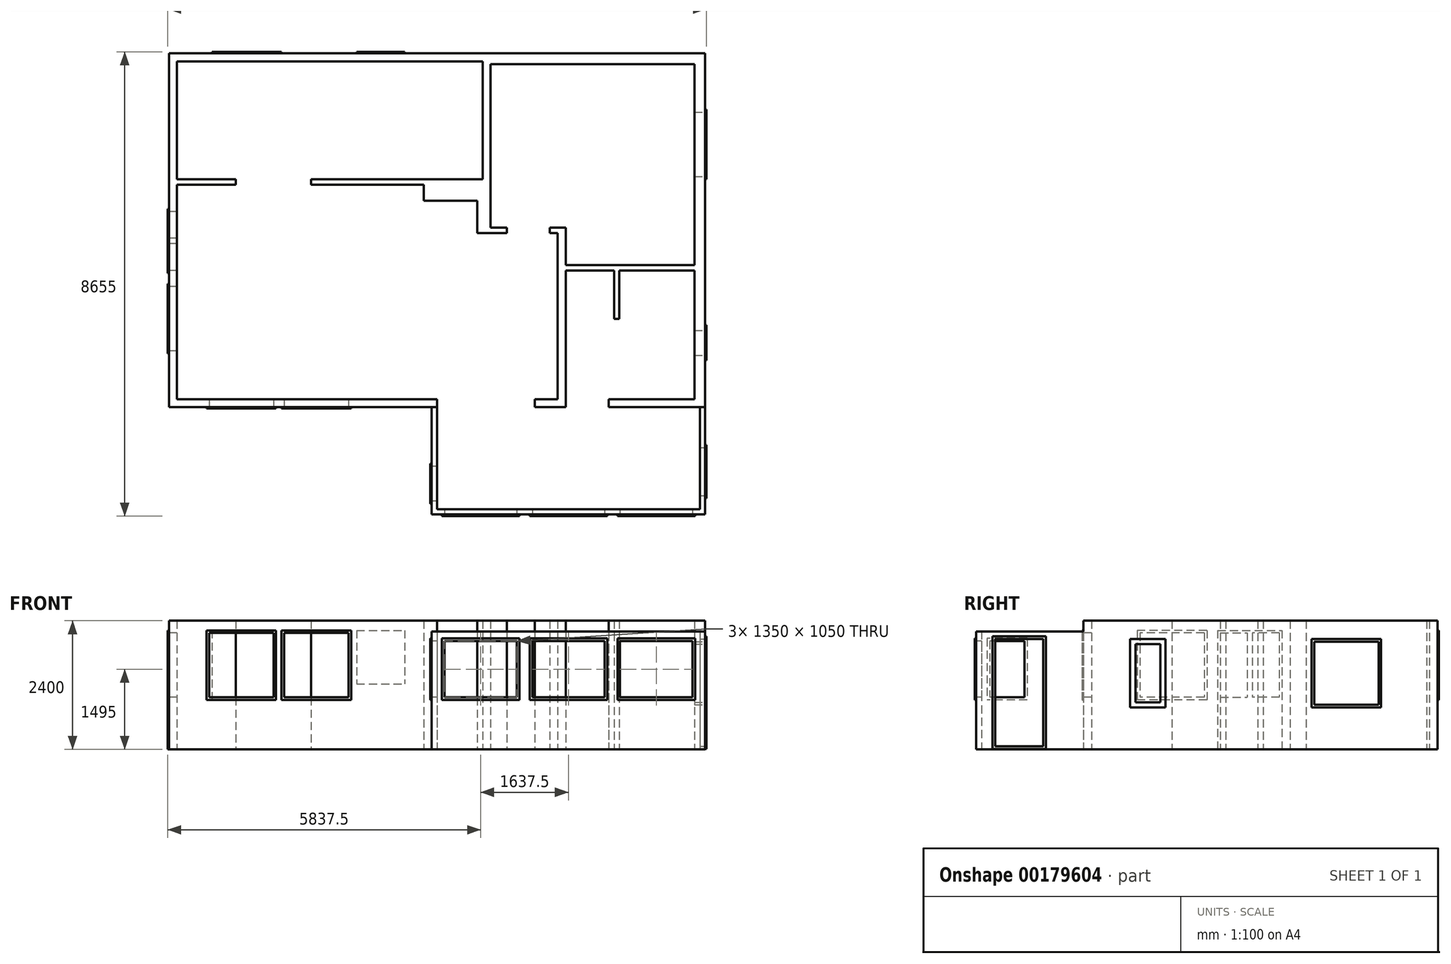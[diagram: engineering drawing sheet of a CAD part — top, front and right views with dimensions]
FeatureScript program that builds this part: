
annotation { "Feature Type Name" : "Feature", "Feature Type Description" : "" }
export const myFeature = defineFeature(function(context is Context, id is Id, definition is map)
    precondition{}
    {
        {
            var Q0;
            Q0=qCreatedBy(makeId("Top.planeOp"),FACE);
            var sketch = newSketch(context, id + "F0", { "sketchPlane" : qUnion([Q0])});
            skLineSegment(sketch, "E0", {"start": v(0, 0) * mm, "end": v(0, 6600) * mm});
            skLineSegment(sketch, "E1", {"start": v(0, 6600) * mm, "end": v(10000, 6600) * mm});
            skLineSegment(sketch, "E2", {"start": v(10000, 6600) * mm, "end": v(10000, 0) * mm});
            skLineSegment(sketch, "E3", {"start": v(10000, 0) * mm, "end": v(8200, 0) * mm});
            skLineSegment(sketch, "E4", {"start": v(8200, 0) * mm, "end": v(8200, 150) * mm});
            skLineSegment(sketch, "E5", {"start": v(8200, 150) * mm, "end": v(9800, 150) * mm});
            skLineSegment(sketch, "E6", {"start": v(9800, 150) * mm, "end": v(9800, 2550) * mm});
            skLineSegment(sketch, "E7", {"start": v(9800, 2550) * mm, "end": v(8400, 2550) * mm});
            skLineSegment(sketch, "E8", {"start": v(8400, 2550) * mm, "end": v(8400, 1650) * mm});
            skLineSegment(sketch, "E9", {"start": v(8400, 1650) * mm, "end": v(8300, 1650) * mm});
            skLineSegment(sketch, "E10", {"start": v(8300, 1650) * mm, "end": v(8300, 2550) * mm});
            skLineSegment(sketch, "E11", {"start": v(8300, 2550) * mm, "end": v(7400, 2550) * mm});
            skLineSegment(sketch, "E12", {"start": v(6820, 150) * mm, "end": v(7250, 150) * mm});
            skLineSegment(sketch, "E13", {"start": v(7250, 150) * mm, "end": v(7250, 3250) * mm});
            skLineSegment(sketch, "E14", {"start": v(7250, 3250) * mm, "end": v(7100, 3250) * mm});
            skLineSegment(sketch, "E15", {"start": v(7100, 3250) * mm, "end": v(7100, 3350) * mm});
            skLineSegment(sketch, "E16", {"start": v(7100, 3350) * mm, "end": v(7400, 3350) * mm});
            skLineSegment(sketch, "E17", {"start": v(7400, 3350) * mm, "end": v(7400, 2650) * mm});
            skLineSegment(sketch, "E18", {"start": v(7400, 2650) * mm, "end": v(9800, 2650) * mm});
            skLineSegment(sketch, "E19", {"start": v(9800, 2650) * mm, "end": v(9800, 6400) * mm});
            skLineSegment(sketch, "E20", {"start": v(6000, 3350) * mm, "end": v(6300, 3350) * mm});
            skLineSegment(sketch, "E21", {"start": v(6300, 3350) * mm, "end": v(6300, 3250) * mm});
            skLineSegment(sketch, "E22", {"start": v(6300, 3250) * mm, "end": v(5750, 3250) * mm});
            skLineSegment(sketch, "E23", {"start": v(5750, 3250) * mm, "end": v(5750, 3850) * mm});
            skLineSegment(sketch, "E24", {"start": v(4750, 3850) * mm, "end": v(4750, 4150) * mm});
            skLineSegment(sketch, "E25", {"start": v(2650, 4250) * mm, "end": v(5850, 4250) * mm});
            skLineSegment(sketch, "E26", {"start": v(5850, 4250) * mm, "end": v(5850, 6450) * mm});
            skLineSegment(sketch, "E27", {"start": v(5850, 6450) * mm, "end": v(150, 6450) * mm});
            skLineSegment(sketch, "E28", {"start": v(150, 6450) * mm, "end": v(150, 4250) * mm});
            skLineSegment(sketch, "E29", {"start": v(150, 4250) * mm, "end": v(1250, 4250) * mm});
            skLineSegment(sketch, "E30", {"start": v(1250, 4250) * mm, "end": v(1250, 4150) * mm});
            skLineSegment(sketch, "E31", {"start": v(1250, 4150) * mm, "end": v(150, 4150) * mm});
            skLineSegment(sketch, "E32", {"start": v(150, 4150) * mm, "end": v(150, 150) * mm});
            skLineSegment(sketch, "E33", {"start": v(150, 150) * mm, "end": v(5000, 150) * mm});
            skLineSegment(sketch, "E34", {"start": v(5000, 150) * mm, "end": v(5000, 0) * mm});
            skLineSegment(sketch, "E35", {"start": v(5000, 0) * mm, "end": v(0, 0) * mm});
            skLineSegment(sketch, "E36", {"start": v(4750, 3850) * mm, "end": v(5750, 3850) * mm});
            skLineSegment(sketch, "E37", {"start": v(6000, 6400) * mm, "end": v(9800, 6400) * mm});
            skLineSegment(sketch, "E38", {"start": v(6000, 6400) * mm, "end": v(6000, 3350) * mm});
            skLineSegment(sketch, "E39", {"start": v(7400, 0) * mm, "end": v(7400, 2550) * mm});
            skLineSegment(sketch, "E40", {"start": v(6820, 150) * mm, "end": v(6820, 0) * mm});
            skLineSegment(sketch, "E41", {"start": v(6820, 0) * mm, "end": v(7400, 0) * mm});
            skLineSegment(sketch, "E42", {"start": v(2650, 4150) * mm, "end": v(4750, 4150) * mm});
            skLineSegment(sketch, "E43", {"start": v(2650, 4250) * mm, "end": v(2650, 4150) * mm});
            skSolve(sketch);
        }
        {
            var Q0;
            Q0 = qSketchRegion(id + "F0", true);
            extrude(context, id + "F1", {"entities" : qUnion([Q0]), "depth" : 2400 * mm});
        }
        {
            var Q0;
            Q0=qCreatedBy(makeId("Top.planeOp"),FACE);
            var sketch = newSketch(context, id + "F2", { "sketchPlane" : qUnion([Q0])});
            skLineSegment(sketch, "E44", {"start": v(10000, 0) * mm, "end": v(10000, -2000) * mm});
            skLineSegment(sketch, "E45", {"start": v(10000, -2000) * mm, "end": v(4900, -2000) * mm});
            skLineSegment(sketch, "E46", {"start": v(4900, -2000) * mm, "end": v(4900, 0) * mm});
            skLineSegment(sketch, "E47", {"start": v(4900, 0) * mm, "end": v(5000, 0) * mm});
            skLineSegment(sketch, "E48", {"start": v(5000, 0) * mm, "end": v(5000, -1900) * mm});
            skLineSegment(sketch, "E49", {"start": v(5000, -1900) * mm, "end": v(9900, -1900) * mm});
            skLineSegment(sketch, "E50", {"start": v(9900, -1900) * mm, "end": v(9900, 0) * mm});
            skLineSegment(sketch, "E51", {"start": v(9900, 0) * mm, "end": v(10000, 0) * mm});
            skSolve(sketch);
        }
        {
            var Q0;
            Q0 = qSketchRegion(id + "F2", true);
            extrude(context, id + "F3", {"entities" : qUnion([Q0]), "operationType" : NewBodyOperationType.ADD, "depth" : 2200 * mm});
        }
        {
            var Q0;
            Q0=makeQuery(id+"F3.opExtrude","SWEPT_FACE",FACE,{"disambiguationData":[OSD([sQuery(id+"F2.wireOp",EDGE,"E45")])]});
            var sketch = newSketch(context, id + "F4", { "sketchPlane" : qUnion([Q0])});
            skLineSegment(sketch, "E52.bottom", {"start": v(6725, 2070) * mm, "end": v(8175, 2070) * mm});
            skLineSegment(sketch, "E52.top", {"start": v(6725, 920) * mm, "end": v(8175, 920) * mm});
            skLineSegment(sketch, "E52.left", {"start": v(6725, 2070) * mm, "end": v(6725, 920) * mm});
            skLineSegment(sketch, "E52.right", {"start": v(8175, 2070) * mm, "end": v(8175, 920) * mm});
            skPoint(sketch, "E53.endSnap0", {"position": v(7450, 2200) * mm});
            skLineSegment(sketch, "E54.bottom", {"start": v(6537.5, 2070) * mm, "end": v(5087.5, 2070) * mm});
            skLineSegment(sketch, "E54.top", {"start": v(6537.5, 920) * mm, "end": v(5087.5, 920) * mm});
            skLineSegment(sketch, "E54.left", {"start": v(6537.5, 2070) * mm, "end": v(6537.5, 920) * mm});
            skLineSegment(sketch, "E54.right", {"start": v(5087.5, 2070) * mm, "end": v(5087.5, 920) * mm});
            skLineSegment(sketch, "E55.bottom", {"start": v(8362.5, 2070) * mm, "end": v(9812.5, 2070) * mm});
            skLineSegment(sketch, "E55.top", {"start": v(8362.5, 920) * mm, "end": v(9812.5, 920) * mm});
            skLineSegment(sketch, "E55.left", {"start": v(8362.5, 2070) * mm, "end": v(8362.5, 920) * mm});
            skLineSegment(sketch, "E55.right", {"start": v(9812.5, 2070) * mm, "end": v(9812.5, 920) * mm});
            skSolve(sketch);
        }
        {
            var Q0;
            Q0=makeQuery(id+"F4.imprint","IMPRINT",FACE,{"disambiguationData":[TD([[makeQuery(id+"F4.imprint","IMPRINT",EDGE,{"derivedFrom":sQuery(id+"F4.wireOp",EDGE,"E54.bottom")}),1.0]])]});
            var Q1;
            Q1=makeQuery(id+"F4.imprint","IMPRINT",FACE,{"disambiguationData":[TD([[makeQuery(id+"F4.imprint","IMPRINT",EDGE,{"derivedFrom":sQuery(id+"F4.wireOp",EDGE,"E52.bottom")}),-1.0]])]});
            var Q2;
            Q2=makeQuery(id+"F4.imprint","IMPRINT",FACE,{"disambiguationData":[TD([[makeQuery(id+"F4.imprint","IMPRINT",EDGE,{"derivedFrom":sQuery(id+"F4.wireOp",EDGE,"E55.bottom")}),-1.0]])]});
            extrude(context, id + "F5", {"entities" : qUnion([Q0, Q1, Q2]), "operationType" : NewBodyOperationType.ADD, "depth" : 30 * mm});
        }
        {
            var Q0;
            Q0=makeQuery(id+"F5.opExtrude","CAP_FACE",FACE,{"disambiguationData":[OSD([sQuery(id+"F4.wireOp",EDGE,"E54.bottom"),sQuery(id+"F4.wireOp",EDGE,"E54.top"),sQuery(id+"F4.wireOp",EDGE,"E54.left"),sQuery(id+"F4.wireOp",EDGE,"E54.right")])],"isStart":false});
            var sketch = newSketch(context, id + "F6", { "sketchPlane" : qUnion([Q0])});
            skLineSegment(sketch, "E56.bottom", {"start": v(5137.5, 2020) * mm, "end": v(6487.5, 2020) * mm});
            skLineSegment(sketch, "E56.top", {"start": v(5137.5, 970) * mm, "end": v(6487.5, 970) * mm});
            skLineSegment(sketch, "E56.left", {"start": v(5137.5, 2020) * mm, "end": v(5137.5, 970) * mm});
            skLineSegment(sketch, "E56.right", {"start": v(6487.5, 2020) * mm, "end": v(6487.5, 970) * mm});
            skLineSegment(sketch, "E57.bottom", {"start": v(6775, 2020) * mm, "end": v(8125, 2020) * mm});
            skLineSegment(sketch, "E57.top", {"start": v(6775, 970) * mm, "end": v(8125, 970) * mm});
            skLineSegment(sketch, "E57.left", {"start": v(6775, 2020) * mm, "end": v(6775, 970) * mm});
            skLineSegment(sketch, "E57.right", {"start": v(8125, 2020) * mm, "end": v(8125, 970) * mm});
            skLineSegment(sketch, "E58.bottom", {"start": v(8412.5, 2020) * mm, "end": v(9762.5, 2020) * mm});
            skLineSegment(sketch, "E58.top", {"start": v(8412.5, 970) * mm, "end": v(9762.5, 970) * mm});
            skLineSegment(sketch, "E58.left", {"start": v(8412.5, 2020) * mm, "end": v(8412.5, 970) * mm});
            skLineSegment(sketch, "E58.right", {"start": v(9762.5, 2020) * mm, "end": v(9762.5, 970) * mm});
            skSolve(sketch);
        }
        {
            var Q0;
            Q0 = qSketchRegion(id + "F6", true);
            extrude(context, id + "F7", {"entities" : qUnion([Q0]), "operationType" : NewBodyOperationType.REMOVE, "endBound" : BoundingType.UP_TO_NEXT, "oppositeDirection" : true, "depth" : 25 * mm});
        }
        {
            var Q0;
            Q0=makeQuery(id+"F3.boolean.opBoolean","MERGE",FACE,{"derivedFrom":[makeQuery(id+"F1.opExtrude","SWEPT_FACE",FACE,{"disambiguationData":[OSD([sQuery(id+"F0.wireOp",EDGE,"E2")])]}),makeQuery(id+"F3.opExtrude","SWEPT_FACE",FACE,{"disambiguationData":[OSD([sQuery(id+"F2.wireOp",EDGE,"E44")])]})]});
            var sketch = newSketch(context, id + "F8", { "sketchPlane" : qUnion([Q0])});
            skLineSegment(sketch, "E59.bottom", {"start": v(-1700, 2110) * mm, "end": v(-700, 2110) * mm});
            skLineSegment(sketch, "E59.top", {"start": v(-1700, 10) * mm, "end": v(-700, 10) * mm});
            skLineSegment(sketch, "E59.left", {"start": v(-1700, 2110) * mm, "end": v(-1700, 10) * mm});
            skLineSegment(sketch, "E59.right", {"start": v(-700, 2110) * mm, "end": v(-700, 10) * mm});
            skSolve(sketch);
        }
        {
            var Q0;
            Q0 = qSketchRegion(id + "F8", true);
            extrude(context, id + "F9", {"entities" : qUnion([Q0]), "operationType" : NewBodyOperationType.ADD, "depth" : 25 * mm});
        }
        {
            var Q0;
            Q0=makeQuery(id+"F9.opExtrude","CAP_FACE",FACE,{"disambiguationData":[OSD([sQuery(id+"F8.wireOp",EDGE,"E59.bottom"),sQuery(id+"F8.wireOp",EDGE,"E59.top"),sQuery(id+"F8.wireOp",EDGE,"E59.left"),sQuery(id+"F8.wireOp",EDGE,"E59.right")])],"isStart":false});
            var sketch = newSketch(context, id + "F10", { "sketchPlane" : qUnion([Q0])});
            skLineSegment(sketch, "E60.bottom", {"start": v(-1650, 2060) * mm, "end": v(-750, 2060) * mm});
            skLineSegment(sketch, "E60.top", {"start": v(-1650, 60) * mm, "end": v(-750, 60) * mm});
            skLineSegment(sketch, "E60.left", {"start": v(-1650, 2060) * mm, "end": v(-1650, 60) * mm});
            skLineSegment(sketch, "E60.right", {"start": v(-750, 2060) * mm, "end": v(-750, 60) * mm});
            skSolve(sketch);
        }
        {
            var Q0;
            Q0 = qSketchRegion(id + "F10", true);
            extrude(context, id + "F11", {"entities" : qUnion([Q0]), "operationType" : NewBodyOperationType.REMOVE, "oppositeDirection" : true, "depth" : 125 * mm});
        }
        {
            var Q0;
            Q0=makeQuery(id+"F3.opExtrude","SWEPT_FACE",FACE,{"disambiguationData":[OSD([sQuery(id+"F2.wireOp",EDGE,"E46")])]});
            var sketch = newSketch(context, id + "F12", { "sketchPlane" : qUnion([Q0])});
            skLineSegment(sketch, "E61.bottom", {"start": v(1050, 2070) * mm, "end": v(1800, 2070) * mm});
            skLineSegment(sketch, "E61.top", {"start": v(1050, 920) * mm, "end": v(1800, 920) * mm});
            skLineSegment(sketch, "E61.left", {"start": v(1050, 2070) * mm, "end": v(1050, 920) * mm});
            skLineSegment(sketch, "E61.right", {"start": v(1800, 2070) * mm, "end": v(1800, 920) * mm});
            skSolve(sketch);
        }
        {
            var Q0;
            Q0 = qSketchRegion(id + "F12", true);
            extrude(context, id + "F13", {"entities" : qUnion([Q0]), "operationType" : NewBodyOperationType.ADD, "depth" : 25 * mm});
        }
        {
            var Q0;
            Q0=makeQuery(id+"F13.opExtrude","CAP_FACE",FACE,{"disambiguationData":[OSD([sQuery(id+"F12.wireOp",EDGE,"E61.bottom"),sQuery(id+"F12.wireOp",EDGE,"E61.top"),sQuery(id+"F12.wireOp",EDGE,"E61.left"),sQuery(id+"F12.wireOp",EDGE,"E61.right")])],"isStart":false});
            var sketch = newSketch(context, id + "F14", { "sketchPlane" : qUnion([Q0])});
            skLineSegment(sketch, "E62.bottom", {"start": v(1100, 2020) * mm, "end": v(1750, 2020) * mm});
            skLineSegment(sketch, "E62.top", {"start": v(1100, 970) * mm, "end": v(1750, 970) * mm});
            skLineSegment(sketch, "E62.left", {"start": v(1100, 2020) * mm, "end": v(1100, 970) * mm});
            skLineSegment(sketch, "E62.right", {"start": v(1750, 2020) * mm, "end": v(1750, 970) * mm});
            skSolve(sketch);
        }
        {
            var Q0;
            Q0 = qSketchRegion(id + "F14", true);
            extrude(context, id + "F15", {"entities" : qUnion([Q0]), "operationType" : NewBodyOperationType.REMOVE, "endBound" : BoundingType.UP_TO_NEXT, "oppositeDirection" : true, "depth" : 25 * mm});
        }
        {
            var Q0;
            Q0=makeQuery(id+"F3.boolean.opBoolean","MERGE",FACE,{"derivedFrom":[makeQuery(id+"F1.opExtrude","SWEPT_FACE",FACE,{"disambiguationData":[OSD([sQuery(id+"F0.wireOp",EDGE,"E2")])]}),makeQuery(id+"F3.opExtrude","SWEPT_FACE",FACE,{"disambiguationData":[OSD([sQuery(id+"F2.wireOp",EDGE,"E44")])]})]});
            var sketch = newSketch(context, id + "F16", { "sketchPlane" : qUnion([Q0])});
            skLineSegment(sketch, "E63.bottom", {"start": v(870, 2060) * mm, "end": v(1530, 2060) * mm});
            skLineSegment(sketch, "E63.top", {"start": v(870, 780) * mm, "end": v(1530, 780) * mm});
            skLineSegment(sketch, "E63.left", {"start": v(870, 2060) * mm, "end": v(870, 780) * mm});
            skLineSegment(sketch, "E63.right", {"start": v(1530, 2060) * mm, "end": v(1530, 780) * mm});
            skSolve(sketch);
        }
        {
            var Q0;
            Q0 = qSketchRegion(id + "F16", true);
            extrude(context, id + "F17", {"entities" : qUnion([Q0]), "operationType" : NewBodyOperationType.ADD, "depth" : 25 * mm});
        }
        {
            var Q0;
            Q0=makeQuery(id+"F17.opExtrude","CAP_FACE",FACE,{"disambiguationData":[OSD([sQuery(id+"F16.wireOp",EDGE,"E63.bottom"),sQuery(id+"F16.wireOp",EDGE,"E63.top"),sQuery(id+"F16.wireOp",EDGE,"E63.left"),sQuery(id+"F16.wireOp",EDGE,"E63.right")])],"isStart":false});
            var sketch = newSketch(context, id + "F18", { "sketchPlane" : qUnion([Q0])});
            skLineSegment(sketch, "E64.bottom", {"start": v(970, 1960) * mm, "end": v(1430, 1960) * mm});
            skLineSegment(sketch, "E64.top", {"start": v(970, 880) * mm, "end": v(1430, 880) * mm});
            skLineSegment(sketch, "E64.left", {"start": v(970, 1960) * mm, "end": v(970, 880) * mm});
            skLineSegment(sketch, "E64.right", {"start": v(1430, 1960) * mm, "end": v(1430, 880) * mm});
            skSolve(sketch);
        }
        {
            var Q0;
            Q0 = qSketchRegion(id + "F18", true);
            extrude(context, id + "F19", {"entities" : qUnion([Q0]), "operationType" : NewBodyOperationType.REMOVE, "endBound" : BoundingType.UP_TO_NEXT, "oppositeDirection" : true, "depth" : 25 * mm});
        }
        {
            var Q0;
            Q0=makeQuery(id+"F3.boolean.opBoolean","MERGE",FACE,{"derivedFrom":[makeQuery(id+"F1.opExtrude","SWEPT_FACE",FACE,{"disambiguationData":[OSD([sQuery(id+"F0.wireOp",EDGE,"E2")])]}),makeQuery(id+"F3.opExtrude","SWEPT_FACE",FACE,{"disambiguationData":[OSD([sQuery(id+"F2.wireOp",EDGE,"E44")])]})]});
            var sketch = newSketch(context, id + "F20", { "sketchPlane" : qUnion([Q0])});
            skLineSegment(sketch, "E65.bottom", {"start": v(5550, 2060) * mm, "end": v(4250, 2060) * mm});
            skLineSegment(sketch, "E65.top", {"start": v(5550, 780) * mm, "end": v(4250, 780) * mm});
            skLineSegment(sketch, "E65.left", {"start": v(5550, 2060) * mm, "end": v(5550, 780) * mm});
            skLineSegment(sketch, "E65.right", {"start": v(4250, 2060) * mm, "end": v(4250, 780) * mm});
            skSolve(sketch);
        }
        {
            var Q0;
            Q0 = qSketchRegion(id + "F20", true);
            extrude(context, id + "F21", {"entities" : qUnion([Q0]), "operationType" : NewBodyOperationType.ADD, "depth" : 25 * mm});
        }
        {
            var Q0;
            Q0=makeQuery(id+"F21.opExtrude","CAP_FACE",FACE,{"disambiguationData":[OSD([sQuery(id+"F20.wireOp",EDGE,"E65.bottom"),sQuery(id+"F20.wireOp",EDGE,"E65.top"),sQuery(id+"F20.wireOp",EDGE,"E65.left"),sQuery(id+"F20.wireOp",EDGE,"E65.right")])],"isStart":false});
            var sketch = newSketch(context, id + "F22", { "sketchPlane" : qUnion([Q0])});
            skLineSegment(sketch, "E66.bottom", {"start": v(4300, 2010) * mm, "end": v(5500, 2010) * mm});
            skLineSegment(sketch, "E66.top", {"start": v(4300, 830) * mm, "end": v(5500, 830) * mm});
            skLineSegment(sketch, "E66.left", {"start": v(4300, 2010) * mm, "end": v(4300, 830) * mm});
            skLineSegment(sketch, "E66.right", {"start": v(5500, 2010) * mm, "end": v(5500, 830) * mm});
            skSolve(sketch);
        }
        {
            var Q0;
            Q0 = qSketchRegion(id + "F22", true);
            extrude(context, id + "F23", {"entities" : qUnion([Q0]), "operationType" : NewBodyOperationType.REMOVE, "endBound" : BoundingType.UP_TO_NEXT, "oppositeDirection" : true, "depth" : 25 * mm});
        }
        {
            var Q0;
            Q0=makeQuery(id+"F1.opExtrude","SWEPT_FACE",FACE,{"disambiguationData":[OSD([sQuery(id+"F0.wireOp",EDGE,"E35")])]});
            var sketch = newSketch(context, id + "F24", { "sketchPlane" : qUnion([Q0])});
            skLineSegment(sketch, "E67.bottom", {"start": v(2100, 2220) * mm, "end": v(3400, 2220) * mm});
            skLineSegment(sketch, "E67.top", {"start": v(2100, 920) * mm, "end": v(3400, 920) * mm});
            skLineSegment(sketch, "E67.left", {"start": v(2100, 2220) * mm, "end": v(2100, 920) * mm});
            skLineSegment(sketch, "E67.right", {"start": v(3400, 2220) * mm, "end": v(3400, 920) * mm});
            skLineSegment(sketch, "E68.bottom", {"start": v(2000, 2220) * mm, "end": v(700, 2220) * mm});
            skLineSegment(sketch, "E68.top", {"start": v(2000, 920) * mm, "end": v(700, 920) * mm});
            skLineSegment(sketch, "E68.left", {"start": v(2000, 2220) * mm, "end": v(2000, 920) * mm});
            skLineSegment(sketch, "E68.right", {"start": v(700, 2220) * mm, "end": v(700, 920) * mm});
            skSolve(sketch);
        }
        {
            var Q0;
            Q0 = qSketchRegion(id + "F24", true);
            extrude(context, id + "F25", {"entities" : qUnion([Q0]), "operationType" : NewBodyOperationType.ADD, "depth" : 25 * mm});
        }
        {
            var Q0;
            Q0=makeQuery(id+"F25.opExtrude","CAP_FACE",FACE,{"disambiguationData":[OSD([sQuery(id+"F24.wireOp",EDGE,"E67.bottom"),sQuery(id+"F24.wireOp",EDGE,"E67.top"),sQuery(id+"F24.wireOp",EDGE,"E67.left"),sQuery(id+"F24.wireOp",EDGE,"E67.right")])],"isStart":false});
            var sketch = newSketch(context, id + "F26", { "sketchPlane" : qUnion([Q0])});
            skLineSegment(sketch, "E69.bottom", {"start": v(2150, 2170) * mm, "end": v(3350, 2170) * mm});
            skLineSegment(sketch, "E69.top", {"start": v(2150, 970) * mm, "end": v(3350, 970) * mm});
            skLineSegment(sketch, "E69.left", {"start": v(2150, 2170) * mm, "end": v(2150, 970) * mm});
            skLineSegment(sketch, "E69.right", {"start": v(3350, 2170) * mm, "end": v(3350, 970) * mm});
            skLineSegment(sketch, "E70.bottom", {"start": v(750, 2170) * mm, "end": v(1950, 2170) * mm});
            skLineSegment(sketch, "E70.top", {"start": v(750, 970) * mm, "end": v(1950, 970) * mm});
            skLineSegment(sketch, "E70.left", {"start": v(750, 2170) * mm, "end": v(750, 970) * mm});
            skLineSegment(sketch, "E70.right", {"start": v(1950, 2170) * mm, "end": v(1950, 970) * mm});
            skSolve(sketch);
        }
        {
            var Q0;
            Q0 = qSketchRegion(id + "F26", true);
            extrude(context, id + "F27", {"entities" : qUnion([Q0]), "operationType" : NewBodyOperationType.REMOVE, "endBound" : BoundingType.UP_TO_NEXT, "oppositeDirection" : true, "depth" : 25 * mm});
        }
        {
            var Q0;
            Q0=makeQuery(id+"F1.opExtrude","SWEPT_FACE",FACE,{"disambiguationData":[OSD([sQuery(id+"F0.wireOp",EDGE,"E1")])]});
            var sketch = newSketch(context, id + "F28", { "sketchPlane" : qUnion([Q0])});
            skLineSegment(sketch, "E71.bottom", {"start": v(-2100, 2220) * mm, "end": v(-800, 2220) * mm});
            skLineSegment(sketch, "E71.top", {"start": v(-2100, 920) * mm, "end": v(-800, 920) * mm});
            skLineSegment(sketch, "E71.left", {"start": v(-2100, 2220) * mm, "end": v(-2100, 920) * mm});
            skLineSegment(sketch, "E71.right", {"start": v(-800, 2220) * mm, "end": v(-800, 920) * mm});
            skLineSegment(sketch, "E72.bottom", {"start": v(-3500, 2220) * mm, "end": v(-4400, 2220) * mm});
            skLineSegment(sketch, "E72.top", {"start": v(-3500, 1220) * mm, "end": v(-4400, 1220) * mm});
            skLineSegment(sketch, "E72.left", {"start": v(-3500, 2220) * mm, "end": v(-3500, 1220) * mm});
            skLineSegment(sketch, "E72.right", {"start": v(-4400, 2220) * mm, "end": v(-4400, 1220) * mm});
            skSolve(sketch);
        }
        {
            var Q0;
            Q0 = qSketchRegion(id + "F28", true);
            var Q1;
            Q1=makeQuery(id+"F28.imprint","IMPRINT",FACE,{"disambiguationData":[TD([[makeQuery(id+"F28.imprint","IMPRINT",EDGE,{"derivedFrom":sQuery(id+"F28.wireOp",EDGE,"E72.bottom")}),1.0]])]});
            extrude(context, id + "F29", {"entities" : qUnion([Q0, Q1]), "operationType" : NewBodyOperationType.ADD, "depth" : 25 * mm});
        }
        {
            var Q0;
            Q0=makeQuery(id+"F1.opExtrude","SWEPT_FACE",FACE,{"disambiguationData":[OSD([sQuery(id+"F0.wireOp",EDGE,"E0")])]});
            var sketch = newSketch(context, id + "F30", { "sketchPlane" : qUnion([Q0])});
            skLineSegment(sketch, "E73.bottom", {"start": v(-2300, 2220) * mm, "end": v(-1000, 2220) * mm});
            skLineSegment(sketch, "E73.top", {"start": v(-2300, 920) * mm, "end": v(-1000, 920) * mm});
            skLineSegment(sketch, "E73.left", {"start": v(-2300, 2220) * mm, "end": v(-2300, 920) * mm});
            skLineSegment(sketch, "E73.right", {"start": v(-1000, 2220) * mm, "end": v(-1000, 920) * mm});
            skLineSegment(sketch, "E74.bottom", {"start": v(-2500, 2220) * mm, "end": v(-3700, 2220) * mm});
            skLineSegment(sketch, "E74.top", {"start": v(-2500, 0) * mm, "end": v(-3700, 0) * mm});
            skLineSegment(sketch, "E74.left", {"start": v(-2500, 2220) * mm, "end": v(-2500, 0) * mm});
            skLineSegment(sketch, "E74.right", {"start": v(-3700, 2220) * mm, "end": v(-3700, 0) * mm});
            skSolve(sketch);
        }
        {
            var Q0;
            Q0 = qSketchRegion(id + "F30", true);
            extrude(context, id + "F31", {"entities" : qUnion([Q0]), "operationType" : NewBodyOperationType.ADD, "depth" : 25 * mm});
        }
        {
            var Q0;
            Q0=makeQuery(id+"F31.opExtrude","CAP_FACE",FACE,{"disambiguationData":[OSD([sQuery(id+"F30.wireOp",EDGE,"E73.bottom"),sQuery(id+"F30.wireOp",EDGE,"E73.top"),sQuery(id+"F30.wireOp",EDGE,"E73.left"),sQuery(id+"F30.wireOp",EDGE,"E73.right")])],"isStart":false});
            var sketch = newSketch(context, id + "F32", { "sketchPlane" : qUnion([Q0])});
            skLineSegment(sketch, "E75.bottom", {"start": v(-2250, 2170) * mm, "end": v(-1050, 2170) * mm});
            skLineSegment(sketch, "E75.top", {"start": v(-2250, 970) * mm, "end": v(-1050, 970) * mm});
            skLineSegment(sketch, "E75.left", {"start": v(-2250, 2170) * mm, "end": v(-2250, 970) * mm});
            skLineSegment(sketch, "E75.right", {"start": v(-1050, 2170) * mm, "end": v(-1050, 970) * mm});
            skLineSegment(sketch, "E76.bottom", {"start": v(-2550, 2170) * mm, "end": v(-3050, 2170) * mm});
            skLineSegment(sketch, "E76.top", {"start": v(-2550, 970) * mm, "end": v(-3050, 970) * mm});
            skLineSegment(sketch, "E76.left", {"start": v(-2550, 2170) * mm, "end": v(-2550, 970) * mm});
            skLineSegment(sketch, "E76.right", {"start": v(-3050, 2170) * mm, "end": v(-3050, 970) * mm});
            skPoint(sketch, "E77.firstSnap0", {"position": v(-2800, 2170) * mm});
            skLineSegment(sketch, "E77.bottom", {"start": v(-3650, 2170) * mm, "end": v(-3150, 2170) * mm});
            skLineSegment(sketch, "E77.top", {"start": v(-3650, 970) * mm, "end": v(-3150, 970) * mm});
            skLineSegment(sketch, "E77.left", {"start": v(-3650, 2170) * mm, "end": v(-3650, 970) * mm});
            skLineSegment(sketch, "E77.right", {"start": v(-3150, 2170) * mm, "end": v(-3150, 970) * mm});
            skSolve(sketch);
        }
        {
            var Q0;
            Q0 = qSketchRegion(id + "F32", true);
            extrude(context, id + "F33", {"entities" : qUnion([Q0]), "operationType" : NewBodyOperationType.REMOVE, "endBound" : BoundingType.UP_TO_NEXT, "oppositeDirection" : true, "depth" : 25 * mm});
        }
    });
